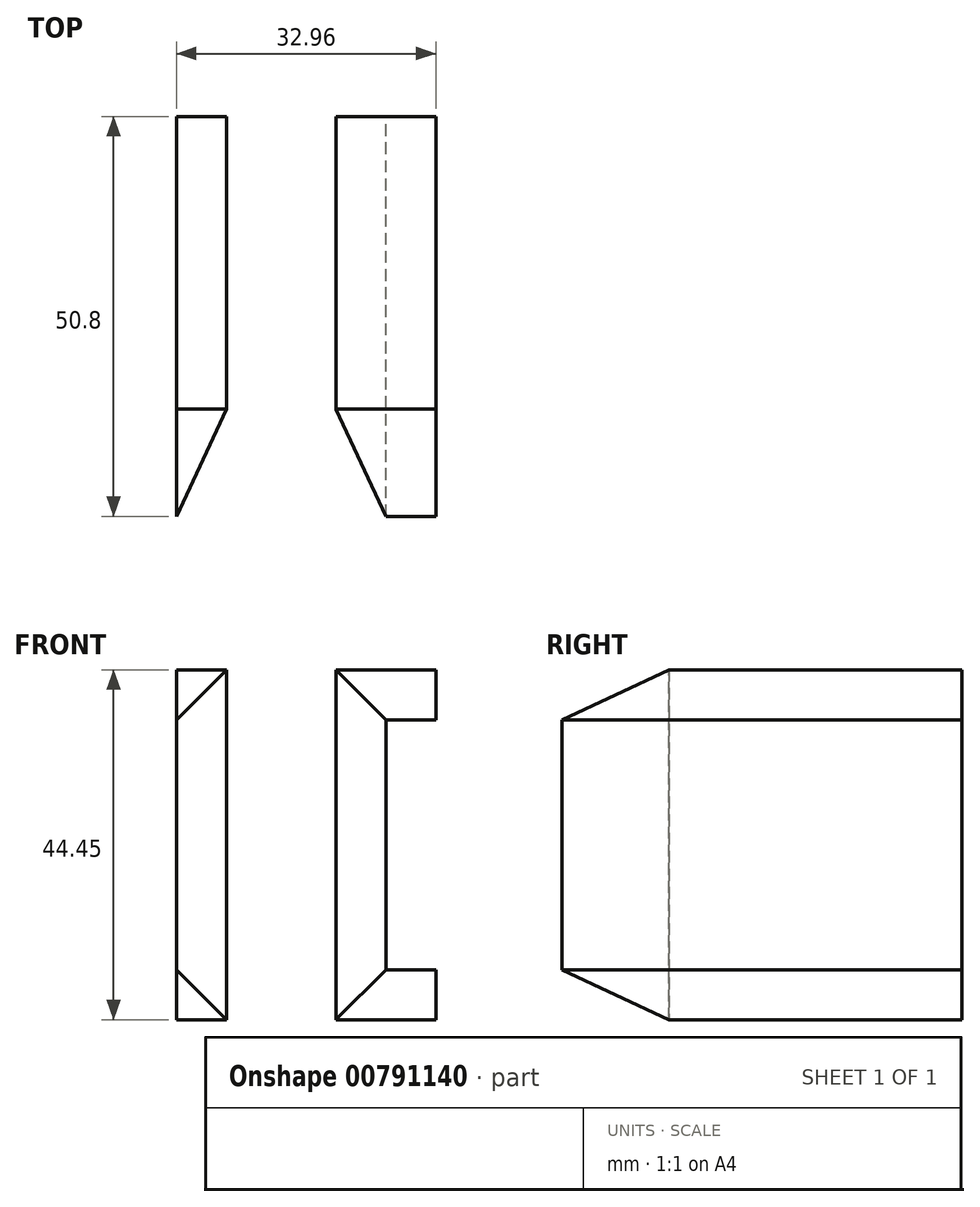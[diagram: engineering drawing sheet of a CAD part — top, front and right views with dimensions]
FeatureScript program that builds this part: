
annotation { "Feature Type Name" : "Feature", "Feature Type Description" : "" }
export const myFeature = defineFeature(function(context is Context, id is Id, definition is map)
    precondition{}
    {
        {
            var Q0;
            Q0=qCreatedBy(makeId("Front.planeOp"),FACE);
            var sketch = newSketch(context, id + "F0", { "sketchPlane" : qUnion([Q0])});
            skLineSegment(sketch, "E0", {"start": v(19.65, 44.45) * mm, "end": v(6.95, 44.45) * mm});
            skLineSegment(sketch, "E1", {"start": v(6.95, 44.45) * mm, "end": v(6.95, 0) * mm});
            skLineSegment(sketch, "E2", {"start": v(6.95, 0) * mm, "end": v(19.65, 0) * mm});
            skLineSegment(sketch, "E3", {"start": v(19.65, 0) * mm, "end": v(19.65, 6.35) * mm});
            skLineSegment(sketch, "E4", {"start": v(19.65, 6.35) * mm, "end": v(13.3, 6.35) * mm});
            skLineSegment(sketch, "E5", {"start": v(13.3, 6.35) * mm, "end": v(13.3, 38.1) * mm});
            skLineSegment(sketch, "E6", {"start": v(13.3, 38.1) * mm, "end": v(19.65, 38.1) * mm});
            skLineSegment(sketch, "E7", {"start": v(19.65, 38.1) * mm, "end": v(19.65, 44.45) * mm});
            skSolve(sketch);
        }
        {
            var Q0;
            Q0 = qSketchRegion(id + "F0", true);
            extrude(context, id + "F1", {"entities" : qUnion([Q0]), "depth" : 50.8 * mm, "offsetDistance" : 25.4 * mm});
        }
        {
            var Q0;
            Q0=qCreatedBy(makeId("Front.planeOp"),FACE);
            var sketch = newSketch(context, id + "F2", { "sketchPlane" : qUnion([Q0])});
            skLineSegment(sketch, "E8", {"start": v(0, 0) * mm, "end": v(-6.96, 0) * mm});
            skLineSegment(sketch, "E9", {"start": v(-6.96, 0) * mm, "end": v(-6.96, 44.45) * mm});
            skLineSegment(sketch, "E10", {"start": v(-6.96, 44.45) * mm, "end": v(-13.3, 44.45) * mm});
            skLineSegment(sketch, "E11", {"start": v(-13.3, 44.45) * mm, "end": v(-13.3, 0) * mm});
            skLineSegment(sketch, "E12", {"start": v(-13.3, 0) * mm, "end": v(-6.96, 0) * mm});
            skSolve(sketch);
        }
        {
            var Q0;
            Q0 = qSketchRegion(id + "F2", true);
            extrude(context, id + "F3", {"entities" : qUnion([Q0]), "depth" : 50.8 * mm, "offsetDistance" : 25.4 * mm});
        }
        {
            var Q0;
            Q0=makeQuery(id+"F1.opExtrude","CAP_EDGE",EDGE,{"disambiguationData":[OSD([sQuery(id+"F0.wireOp",EDGE,"E1")])],"isStart":false});
            chamfer(context, id + "F4", {"entities" : qUnion([Q0]), "chamferType" : ChamferType.OFFSET_ANGLE, "width" : 13.6 * mm, "oppositeDirection" : true, "angle" : 25 * degree, "tangentPropagation" : true});
        }
        {
            var Q0;
            Q0=makeQuery(id+"F1.opExtrude","CAP_EDGE",EDGE,{"disambiguationData":[OSD([sQuery(id+"F0.wireOp",EDGE,"E2")])],"isStart":false});
            chamfer(context, id + "F5", {"entities" : qUnion([Q0]), "chamferType" : ChamferType.OFFSET_ANGLE, "width" : 6.35 * mm, "oppositeDirection" : false, "angle" : 65 * degree, "tangentPropagation" : true});
        }
        {
            var Q0;
            Q0=makeQuery(id+"F1.opExtrude","CAP_EDGE",EDGE,{"disambiguationData":[OSD([sQuery(id+"F0.wireOp",EDGE,"E0")])],"isStart":false});
            chamfer(context, id + "F6", {"entities" : qUnion([Q0]), "chamferType" : ChamferType.OFFSET_ANGLE, "width" : 6.35 * mm, "oppositeDirection" : false, "angle" : 65 * degree, "tangentPropagation" : true});
        }
        {
            var Q0;
            Q0=makeQuery(id+"F3.opExtrude","CAP_EDGE",EDGE,{"disambiguationData":[OSD([sQuery(id+"F2.wireOp",EDGE,"E9")])],"isStart":false});
            var Q1;
            Q1=makeQuery(id+"F3.opExtrude","CAP_EDGE",EDGE,{"disambiguationData":[OSD([sQuery(id+"F2.wireOp",EDGE,"E10")])],"isStart":false});
            var Q2;
            Q2=makeQuery(id+"F3.opExtrude","CAP_EDGE",EDGE,{"disambiguationData":[OSD([sQuery(id+"F2.wireOp",EDGE,"E12")])],"isStart":false});
            chamfer(context, id + "F7", {"entities" : qUnion([Q0, Q1, Q2]), "chamferType" : ChamferType.OFFSET_ANGLE, "width" : 6.35 * mm, "oppositeDirection" : false, "angle" : 65 * degree, "tangentPropagation" : true});
        }
    });
